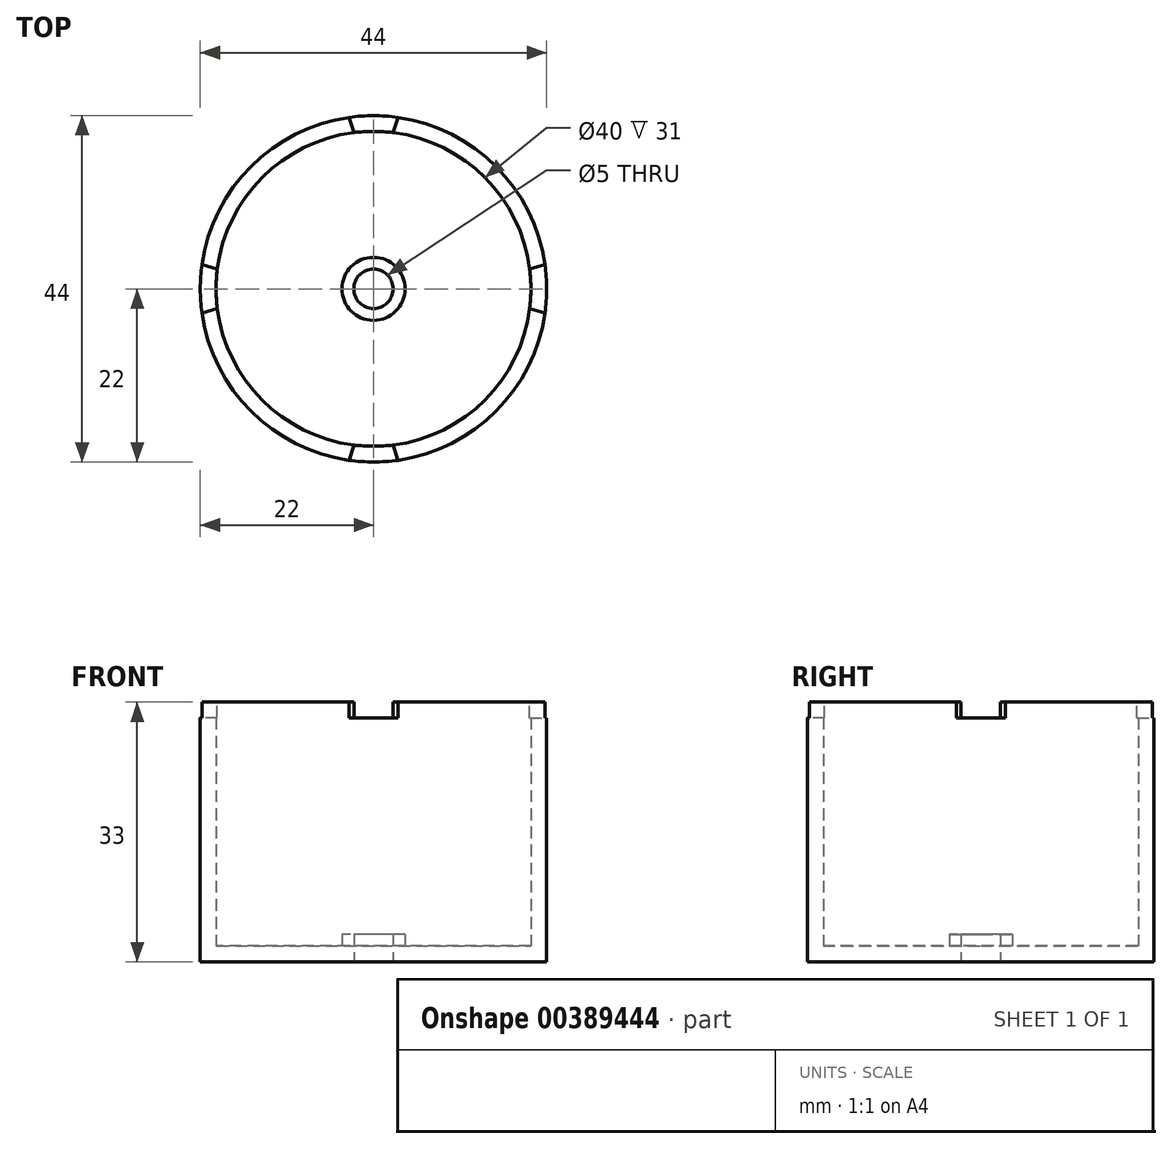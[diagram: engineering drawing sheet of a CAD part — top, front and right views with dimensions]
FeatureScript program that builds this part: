
annotation { "Feature Type Name" : "Feature", "Feature Type Description" : "" }
export const myFeature = defineFeature(function(context is Context, id is Id, definition is map)
    precondition{}
    {
        {
            var Q0;
            Q0=qCreatedBy(makeId("Top.planeOp"),FACE);
            var sketch = newSketch(context, id + "F0", { "sketchPlane" : qUnion([Q0])});
            skCircle(sketch, "E0", {"center": v(0, 0) * mm, "radius": 20 * mm});
            skCircle(sketch, "E1", {"center": v(0, 0) * mm, "radius": 22 * mm});
            skSolve(sketch);
        }
        {
            var Q0;
            Q0=makeQuery(id+"F0.imprint","IMPRINT",FACE,{"disambiguationData":[TD([[makeQuery(id+"F0.imprint","IMPRINT",EDGE,{"derivedFrom":sQuery(id+"F0.wireOp",EDGE,"E0")}),-1.0]])]});
            extrude(context, id + "F1", {"entities" : qUnion([Q0]), "depth" : 33 * mm});
        }
        {
            var Q0;
            Q0=qCreatedBy(makeId("Top.planeOp"),FACE);
            var sketch = newSketch(context, id + "F2", { "sketchPlane" : qUnion([Q0])});
            skCircle(sketch, "E2", {"center": v(0, 0) * mm, "radius": 22 * mm});
            skCircle(sketch, "E3", {"center": v(0, 0) * mm, "radius": 2.5 * mm});
            skSolve(sketch);
        }
        {
            var Q0;
            Q0=makeQuery(id+"F2.imprint","IMPRINT",FACE,{"disambiguationData":[TD([[makeQuery(id+"F2.imprint","IMPRINT",EDGE,{"derivedFrom":sQuery(id+"F2.wireOp",EDGE,"E2")}),1.0]])]});
            extrude(context, id + "F3", {"entities" : qUnion([Q0]), "operationType" : NewBodyOperationType.ADD, "depth" : 2 * mm});
        }
        {
            var Q0;
            Q0=makeQuery(id+"F1.opExtrude","CAP_FACE",FACE,{"disambiguationData":[OSD([sQuery(id+"F0.wireOp",EDGE,"E0"),sQuery(id+"F0.wireOp",EDGE,"E1")])],"isStart":false});
            var sketch = newSketch(context, id + "F4", { "sketchPlane" : qUnion([Q0])});
            skArc(sketch, "E4", {"start": v(-2.5, 19.84) * mm, "mid": v(-1.25, 19.96) * mm, "end": v(0, 20) * mm});
            skArc(sketch, "E5", {"start": v(0, 20) * mm, "mid": v(1.25, 19.96) * mm, "end": v(2.5, 19.84) * mm});
            skLineSegment(sketch, "E6", {"start": v(-2.5, 19.84) * mm, "end": v(-3.1, 21.8) * mm});
            skLineSegment(sketch, "E7", {"start": v(3.1, 21.8) * mm, "end": v(2.5, 19.84) * mm});
            skArc(sketch, "E8", {"start": v(-3.1, 21.8) * mm, "mid": v(0, 22.02) * mm, "end": v(3.1, 21.8) * mm});
            skLineSegment(sketch, "E9.1.0", {"start": v(-19.84, -2.5) * mm, "end": v(-21.8, -3.1) * mm});
            skArc(sketch, "E9.1.1", {"start": v(-21.8, -3.1) * mm, "mid": v(-22.02, 0) * mm, "end": v(-21.8, 3.1) * mm});
            skArc(sketch, "E9.1.2", {"start": v(-20, 0) * mm, "mid": v(-19.96, 1.25) * mm, "end": v(-19.84, 2.5) * mm});
            skArc(sketch, "E9.1.3", {"start": v(-19.84, -2.5) * mm, "mid": v(-19.96, -1.25) * mm, "end": v(-20, 0) * mm});
            skLineSegment(sketch, "E9.1.4", {"start": v(-21.8, 3.1) * mm, "end": v(-19.84, 2.5) * mm});
            skLineSegment(sketch, "E9.2.0", {"start": v(2.5, -19.84) * mm, "end": v(3.1, -21.8) * mm});
            skArc(sketch, "E9.2.1", {"start": v(3.1, -21.8) * mm, "mid": v(0, -22.02) * mm, "end": v(-3.1, -21.8) * mm});
            skArc(sketch, "E9.2.2", {"start": v(0, -20) * mm, "mid": v(-1.25, -19.96) * mm, "end": v(-2.5, -19.84) * mm});
            skArc(sketch, "E9.2.3", {"start": v(2.5, -19.84) * mm, "mid": v(1.25, -19.96) * mm, "end": v(0, -20) * mm});
            skLineSegment(sketch, "E9.2.4", {"start": v(-3.1, -21.8) * mm, "end": v(-2.5, -19.84) * mm});
            skLineSegment(sketch, "E9.3.0", {"start": v(19.84, 2.5) * mm, "end": v(21.8, 3.1) * mm});
            skArc(sketch, "E9.3.1", {"start": v(21.8, 3.1) * mm, "mid": v(22.02, 0) * mm, "end": v(21.8, -3.1) * mm});
            skArc(sketch, "E9.3.2", {"start": v(20, 0) * mm, "mid": v(19.96, -1.25) * mm, "end": v(19.84, -2.5) * mm});
            skArc(sketch, "E9.3.3", {"start": v(19.84, 2.5) * mm, "mid": v(19.96, 1.25) * mm, "end": v(20, 0) * mm});
            skLineSegment(sketch, "E9.3.4", {"start": v(21.8, -3.1) * mm, "end": v(19.84, -2.5) * mm});
            skSolve(sketch);
        }
        {
            var Q0;
            Q0=qSketchRegion(id+"F4",true);
            extrude(context, id + "F5", {"entities" : qUnion([Q0]), "operationType" : NewBodyOperationType.REMOVE, "oppositeDirection" : true, "depth" : 2 * mm});
        }
        {
            var Q0;
            Q0=makeQuery(id+"F3.opExtrude","CAP_FACE",FACE,{"disambiguationData":[OSD([sQuery(id+"F2.wireOp",EDGE,"E2"),sQuery(id+"F2.wireOp",EDGE,"E3")])],"isStart":false});
            var sketch = newSketch(context, id + "F6", { "sketchPlane" : qUnion([Q0])});
            skCircle(sketch, "E10", {"center": v(0, 0) * mm, "radius": 2.5 * mm});
            skCircle(sketch, "E11", {"center": v(0, 0) * mm, "radius": 4 * mm});
            skSolve(sketch);
        }
        {
            var Q0;
            Q0=qSketchRegion(id+"F6",true);
            extrude(context, id + "F7", {"entities" : qUnion([Q0]), "operationType" : NewBodyOperationType.ADD, "depth" : 1.5 * mm});
        }
    });
